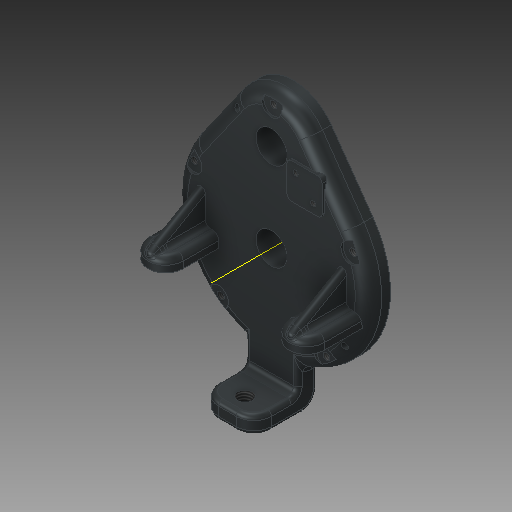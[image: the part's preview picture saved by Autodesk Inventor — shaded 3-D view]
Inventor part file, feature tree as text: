
AUTODESK INVENTOR PART (.ipt)
format: ipt  version: 2020 (Build 240168000, 168)  size: 699,392 bytes
history: native  units: in
note: dims shown in document units (in); Inventor stores cm internally (conversion verified against a paired STEP export)
features: fillet x9, sketch x9, extrude x6, hole x5, reference x5, plane x3, projected_geometry x2, rib x1, mirror x1, other x1
ambient origin geometry x8: Origin, YZ Plane, XZ Plane, XY Plane, X Axis, Y Axis, Z Axis, Center Point
bodies: Solid1 (feature_tree)
feature tree (42):
  plane  "Work Plane1"
  extrude  "Extrusion1"  Depth=1.375in
  extrude  "Extrusion2"  Depth=0.4966in
  extrude  "Extrusion3"  Depth=1.0625in
  plane  "Work Plane2"
  rib  "Rib1"
  fillet  "Fillet5"  Radius=2.5in
  fillet  "Fillet6"  Radius=0.1875in
  fillet  "Fillet7"  Radius=0.8015in
  fillet  "Fillet8"  Radius=2.5in
  fillet  "Fillet9"  Radius=0.375in
  mirror  "Mirror1"
  extrude  "Extrusion4"  Depth=1.5in
  other  "Work Axis1"
  extrude  "Extrusion5"  Depth=2.25in
  extrude  "Extrusion6"  Depth=2.5in
  fillet  "Fillet10"  Radius=2.937in
  fillet  "Fillet11"  Radius=1.0in
  fillet  "Fillet12"  Radius=1.375in
  fillet  "Fillet13"  Radius=2.062in
  hole  "Hole1"  [1 undecoded]
  hole  "Hole2"  [1 undecoded]
  hole  "Hole3"  [1 undecoded]
  hole  "Hole4"  [1 undecoded]
  hole  "Hole5"  [1 undecoded]
  sketch  "Sketch1"  dims[d0=0.625in d1=0.0in d2=1.375in]
  reference  "Reference1"
  reference  "Reference2"
  reference  "Reference3"
  reference  "Reference4"
  projected_geometry  "Projected Loop1"
  sketch  "Sketch3"  dims[d3=2.5in d10=0.4966in]
  sketch  "Sketch4"  dims[d17=2.5in d18=1.0625in d19=1.0625in d21=2.5in d24=0.1875in d25=0.8015in d28=2.5in d29=0.375in d30=0.0in]
  plane  "Work Plane3"
  sketch  "Sketch5"  dims[d31=1.9375in d32=1.5in]
  sketch  "Sketch6"  dims[d33=1.0in d34=2.25in]
  sketch  "Sketch7"  dims[d35=0.25in d36=2.5in d37=2.937in d38=1.0in d39=1.375in d40=2.062in]
  sketch  "Sketch9"  dims[d41=0.1875in d43=1.0in]
  projected_geometry  "Projected Loop2"
  sketch  "Sketch10"  dims[d44=0.5in d45=2.0in]
  sketch  "Sketch11"  dims[d46=0.375in d47=0.75in d48=1.5in d49=0.0in d50=0.625in d51=30.0deg d52=0.1in d53=0.25in d54=0.0in d55=0.0in d56=0.1in d57=0.1in d61=0.1875in d62=0.125in d63=0.125in d64=1.0in d65=1.0in d66=0.5in d67=2.5in d68=0.125in d73=0.0625in d74=0.0in d75=0.5625in d76=0.5in d77=1.25in d78=0.4375in d79=0.1875in d80=3.75in d81=1.5in d82=0.0in d83=1.5in d84=0.0in d85=0.5in d86=0.375in d87=0.125in d88=0.1875in d89=0.196in d90=0.5in d91=0.5625in d92=0.0625in d93=0.5635in d94=0.625in d95=0.8108in d96=0.25in d97=0.25in d98=0.75in d99=0.75in d100=0.145in d101=0.38in d102=0.375in d103=0.25in d104=0.5635in d105=0.588in d106=0.8108in d107=0.75in d108=1.375in d109=0.417in d110=1.0in d111=0.375in d112=0.25in d113=0.5635in d114=1.385in d115=0.8108in d116=0.875in d117=1.0in d118=0.375in d119=0.25in d120=0.5635in d121=1.385in d122=0.8108in d123=0.172in d124=1.0in d125=0.375in d126=0.25in d127=0.5635in d128=1.385in d129=0.8108in d131=3.5in]
  reference  "Reference5"
note: 5 required parameter values undecoded (feature->parameter linkage not recoverable at this tier; creation-order binding heuristic only, values carry confidence <= 0.55)
